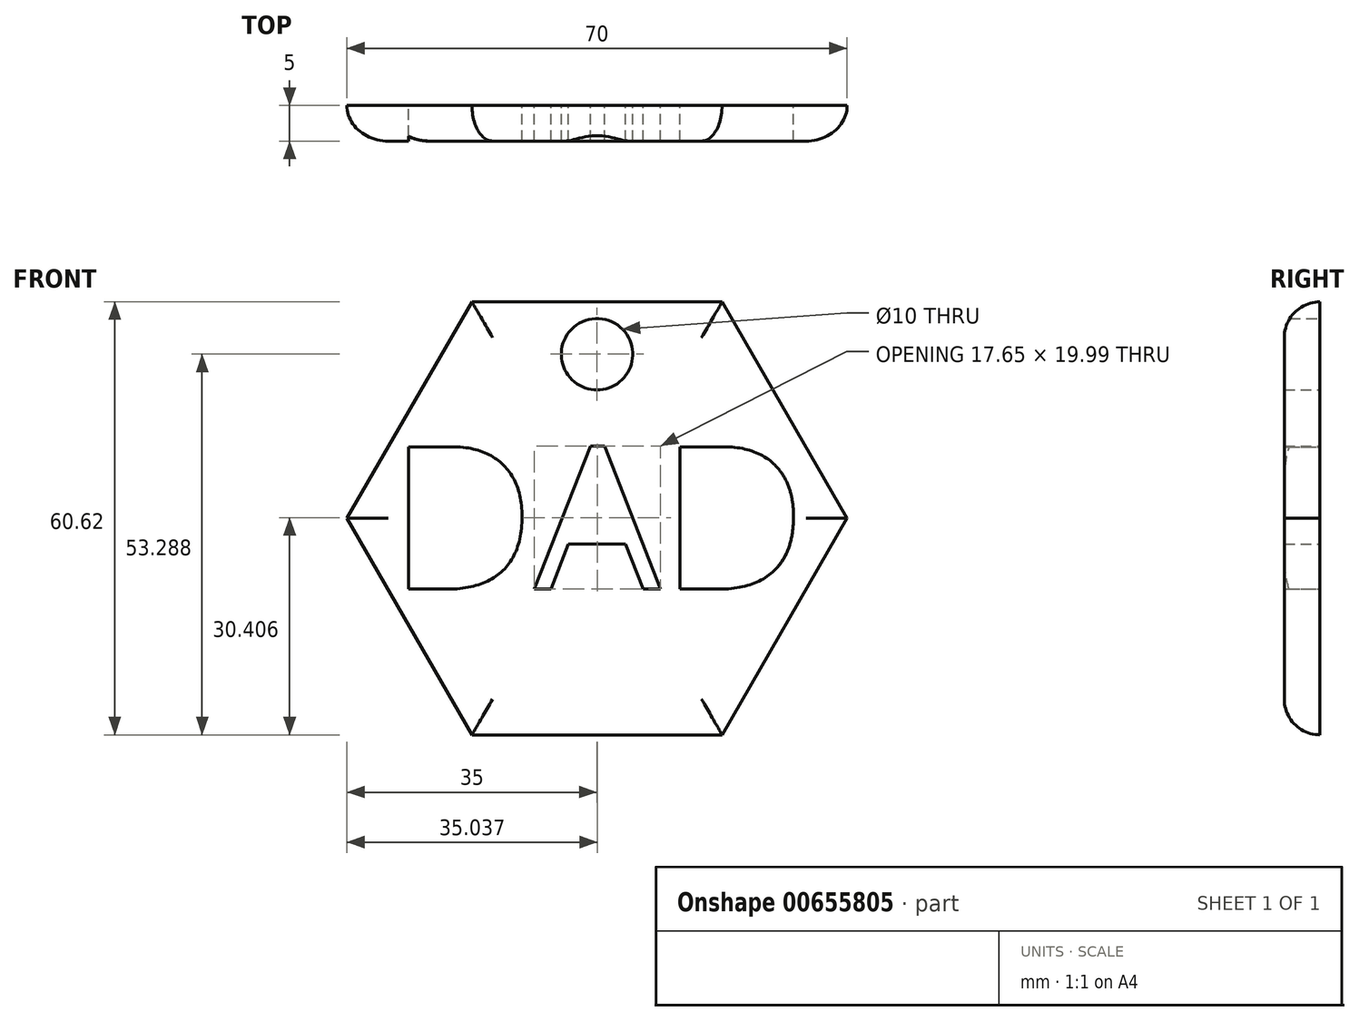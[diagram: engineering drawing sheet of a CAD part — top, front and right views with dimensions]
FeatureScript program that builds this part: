
annotation { "Feature Type Name" : "Feature", "Feature Type Description" : "" }
export const myFeature = defineFeature(function(context is Context, id is Id, definition is map)
    precondition{}
    {
        {
            var Q0;
            Q0=qCreatedBy(makeId("Front.planeOp"),FACE);
            var sketch = newSketch(context, id + "F0", { "sketchPlane" : qUnion([Q0])});
            skCircle(sketch, "E0.cCircle", {"center": v(0, 0) * mm, "radius": 30.31 * mm, "construction": true});
            skLineSegment(sketch, "E0.0", {"start": v(17.5, 30.31) * mm, "end": v(35, 0) * mm});
            skLineSegment(sketch, "E0.1", {"start": v(35, 0) * mm, "end": v(17.5, -30.31) * mm});
            skLineSegment(sketch, "E0.2", {"start": v(17.5, -30.31) * mm, "end": v(-17.5, -30.31) * mm});
            skLineSegment(sketch, "E0.3", {"start": v(-17.5, -30.31) * mm, "end": v(-35, 0) * mm});
            skLineSegment(sketch, "E0.4", {"start": v(-35, 0) * mm, "end": v(-17.5, 30.31) * mm});
            skLineSegment(sketch, "E0.5", {"start": v(-17.5, 30.31) * mm, "end": v(17.5, 30.31) * mm});
            skPoint(sketch, "E0.0.midPoint", {"position": v(26.25, 15.16) * mm});
            skText(sketch, "E1", { "text": "DAD", "fontName": "OpenSans-Regular.ttf"});
            skCircle(sketch, "E2", {"center": v(0, 22.98) * mm, "radius": 5 * mm});
            skLineSegment(sketch, "E3", {"start": v(0, -30.31) * mm, "end": v(0, 0) * mm});
            skLineSegment(sketch, "E4", {"start": v(0, 0) * mm, "end": v(0, 0) * mm});
            skLineSegment(sketch, "E5", {"start": v(-0.14, 0.09) * mm, "end": v(-0.14, 0.09) * mm});
            const initialGuessF0  = {"E1": [-0.02912, -0.0099, 1, 0, 0.02008]};
            skSetInitialGuess(sketch, initialGuessF0);
            skSolve(sketch);
        }
        {
            var Q0;
            Q0=makeQuery(id+"F0.imprint","IMPRINT",FACE,{"disambiguationData":[TD([[makeQuery(id+"F0.imprint","IMPRINT",EDGE,{"derivedFrom":sQuery(id+"F0.wireOp",EDGE,"E1.sketch_text.stroke-22")}),1.0]])]});
            var Q1;
            Q1=makeQuery(id+"F0.imprint","IMPRINT",FACE,{"disambiguationData":[TD([[makeQuery(id+"F0.imprint","IMPRINT",EDGE,{"derivedFrom":sQuery(id+"F0.wireOp",EDGE,"E1.sketch_text.stroke-34")}),1.0]])]});
            var Q2;
            Q2=makeQuery(id+"F0.imprint","IMPRINT",FACE,{"disambiguationData":[TD([[makeQuery(id+"F0.imprint","IMPRINT",EDGE,{"derivedFrom":sQuery(id+"F0.wireOp",EDGE,"E0.0")}),-1.0]])]});
            var Q3;
            Q3=makeQuery(id+"F0.imprint","IMPRINT",FACE,{"disambiguationData":[TD([[makeQuery(id+"F0.imprint","IMPRINT",EDGE,{"derivedFrom":sQuery(id+"F0.wireOp",EDGE,"E1.sketch_text.stroke-7")}),1.0]])]});
            extrude(context, id + "F1", {"entities" : qUnion([Q0, Q1, Q2, Q3]), "depth" : 5 * mm, "offsetDistance" : 25 * mm});
        }
        {
            var Q0;
            Q0=makeQuery(id+"F1.opExtrude","CAP_EDGE",EDGE,{"disambiguationData":[OSD([sQuery(id+"F0.wireOp",EDGE,"E0.4")])],"isStart":false});
            var Q1;
            Q1=makeQuery(id+"F1.opExtrude","CAP_EDGE",EDGE,{"disambiguationData":[OSD([sQuery(id+"F0.wireOp",EDGE,"E0.5")])],"isStart":false});
            var Q2;
            Q2=makeQuery(id+"F1.opExtrude","CAP_EDGE",EDGE,{"disambiguationData":[OSD([sQuery(id+"F0.wireOp",EDGE,"E0.0")])],"isStart":false});
            var Q3;
            Q3=makeQuery(id+"F1.opExtrude","CAP_EDGE",EDGE,{"disambiguationData":[OSD([sQuery(id+"F0.wireOp",EDGE,"E0.1")])],"isStart":false});
            var Q4;
            Q4=makeQuery(id+"F1.opExtrude","CAP_EDGE",EDGE,{"disambiguationData":[OSD([sQuery(id+"F0.wireOp",EDGE,"E0.3")])],"isStart":false});
            var Q5;
            Q5=makeQuery(id+"F1.opExtrude","CAP_EDGE",EDGE,{"disambiguationData":[OSD([sQuery(id+"F0.wireOp",EDGE,"E0.2")])],"isStart":false});
            fillet(context, id + "F2", {"entities" : qUnion([Q0, Q1, Q2, Q3, Q4, Q5]), "radius" : 5 * mm, "tangentPropagation" : true, "allowEdgeOverflow" : false});
        }
        {
            var Q0;
            Q0=makeQuery(id+"F1.opExtrude","SWEPT_BODY",BODY,{"disambiguationData":[OSD([sQuery(id+"F0.wireOp",EDGE,"E1.sketch_text.stroke-7"),sQuery(id+"F0.wireOp",EDGE,"E1.sketch_text.stroke-8"),sQuery(id+"F0.wireOp",EDGE,"E1.sketch_text.stroke-9"),sQuery(id+"F0.wireOp",EDGE,"E1.sketch_text.stroke-10"),sQuery(id+"F0.wireOp",EDGE,"E1.sketch_text.stroke-11"),sQuery(id+"F0.wireOp",EDGE,"E1.sketch_text.stroke-12"),sQuery(id+"F0.wireOp",EDGE,"E1.sketch_text.stroke-13")])]});
            deleteBodies(context, id + "F3", {"entities" : qUnion([Q0])});
        }
        {
            var Q0;
            Q0=makeQuery(id+"F1.opExtrude","SWEPT_BODY",BODY,{"disambiguationData":[OSD([sQuery(id+"F0.wireOp",EDGE,"E1.sketch_text.stroke-22"),sQuery(id+"F0.wireOp",EDGE,"E1.sketch_text.stroke-23"),sQuery(id+"F0.wireOp",EDGE,"E1.sketch_text.stroke-24"),sQuery(id+"F0.wireOp",EDGE,"E1.sketch_text.stroke-25"),sQuery(id+"F0.wireOp",EDGE,"E1.sketch_text.stroke-26")])]});
            deleteBodies(context, id + "F4", {"entities" : qUnion([Q0])});
        }
        {
            var Q0;
            Q0=makeQuery(id+"F1.opExtrude","SWEPT_BODY",BODY,{"disambiguationData":[OSD([sQuery(id+"F0.wireOp",EDGE,"E1.sketch_text.stroke-34"),sQuery(id+"F0.wireOp",EDGE,"E1.sketch_text.stroke-35"),sQuery(id+"F0.wireOp",EDGE,"E1.sketch_text.stroke-36"),sQuery(id+"F0.wireOp",EDGE,"E1.sketch_text.stroke-37"),sQuery(id+"F0.wireOp",EDGE,"E1.sketch_text.stroke-38"),sQuery(id+"F0.wireOp",EDGE,"E1.sketch_text.stroke-39"),sQuery(id+"F0.wireOp",EDGE,"E1.sketch_text.stroke-40")])]});
            deleteBodies(context, id + "F5", {"entities" : qUnion([Q0])});
        }
    });
